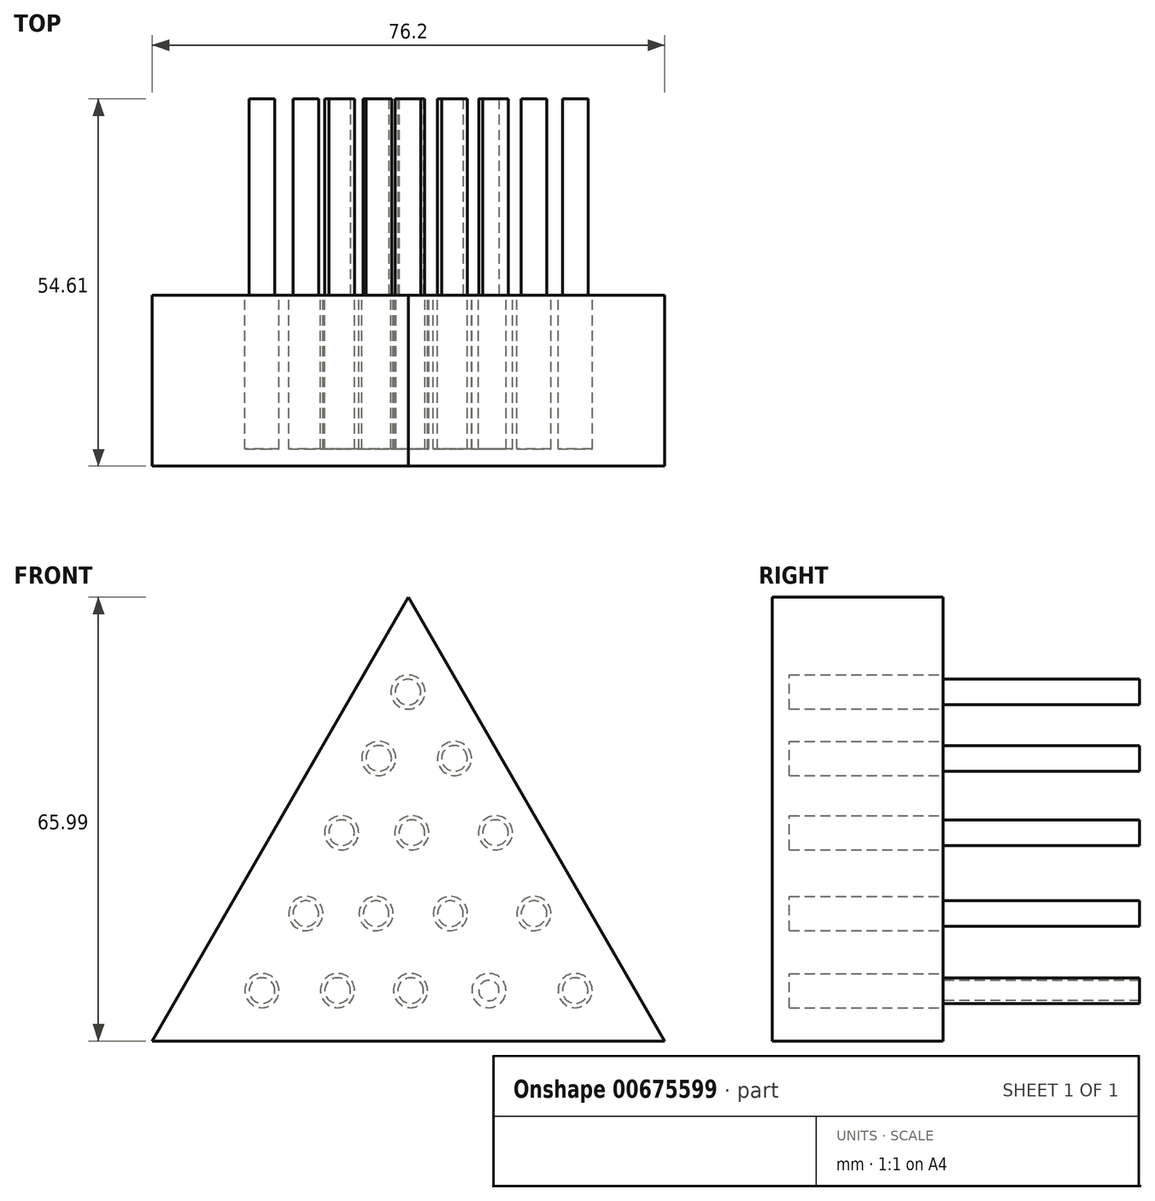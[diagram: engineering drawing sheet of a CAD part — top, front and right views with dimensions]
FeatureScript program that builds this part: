
annotation { "Feature Type Name" : "Feature", "Feature Type Description" : "" }
export const myFeature = defineFeature(function(context is Context, id is Id, definition is map)
    precondition{}
    {
        {
            var Q0;
            Q0=qCreatedBy(makeId("Front.planeOp"),FACE);
            var sketch = newSketch(context, id + "F0", { "sketchPlane" : qUnion([Q0])});
            skLineSegment(sketch, "E0", {"start": v(-76.2, 0) * mm, "end": v(0, 0) * mm});
            skLineSegment(sketch, "E1", {"start": v(0, 0) * mm, "end": v(-38.1, 66) * mm});
            skPoint(sketch, "E1.endSnap0", {"position": v(-38.1, 0) * mm});
            skLineSegment(sketch, "E2", {"start": v(-38.1, 66) * mm, "end": v(-76.2, 0) * mm});
            skSolve(sketch);
        }
        {
            var Q0;
            Q0 = qSketchRegion(id + "F0", true);
            extrude(context, id + "F1", {"entities" : qUnion([Q0]), "depth" : 25.4 * mm, "offsetDistance" : 25.4 * mm});
        }
        {
            var Q0;
            Q0=qCreatedBy(makeId("Front.planeOp"),FACE);
            var sketch = newSketch(context, id + "F2", { "sketchPlane" : qUnion([Q0])});
            skCircle(sketch, "E3", {"center": v(-37.79, 7.5) * mm, "radius": 2.54 * mm});
            skCircle(sketch, "E4", {"center": v(-48.64, 7.5) * mm, "radius": 2.54 * mm});
            skCircle(sketch, "E5", {"center": v(-26.14, 7.5) * mm, "radius": 2.54 * mm});
            skCircle(sketch, "E6", {"center": v(-59.88, 7.5) * mm, "radius": 2.54 * mm});
            skCircle(sketch, "E7", {"center": v(-13.32, 7.5) * mm, "radius": 2.54 * mm});
            skSolve(sketch);
        }
        {
            var Q0;
            Q0 = qSketchRegion(id + "F2", true);
            extrude(context, id + "F3", {"entities" : qUnion([Q0]), "operationType" : NewBodyOperationType.REMOVE, "depth" : 22.86 * mm, "offsetDistance" : 25.4 * mm});
        }
        {
            var Q0;
            Q0=qCreatedBy(makeId("Front.planeOp"),FACE);
            var sketch = newSketch(context, id + "F4", { "sketchPlane" : qUnion([Q0])});
            skCircle(sketch, "E8", {"center": v(-31.87, 18.94) * mm, "radius": 2.54 * mm});
            skCircle(sketch, "E9", {"center": v(-19.44, 18.94) * mm, "radius": 2.54 * mm});
            skCircle(sketch, "E10", {"center": v(-42.92, 18.94) * mm, "radius": 2.54 * mm});
            skCircle(sketch, "E11", {"center": v(-53.37, 18.94) * mm, "radius": 2.54 * mm});
            skSolve(sketch);
        }
        {
            var Q0;
            Q0 = qSketchRegion(id + "F4", true);
            extrude(context, id + "F5", {"entities" : qUnion([Q0]), "operationType" : NewBodyOperationType.REMOVE, "depth" : 22.86 * mm, "offsetDistance" : 25.4 * mm});
        }
        {
            var Q0;
            Q0=qCreatedBy(makeId("Front.planeOp"),FACE);
            var sketch = newSketch(context, id + "F6", { "sketchPlane" : qUnion([Q0])});
            skCircle(sketch, "E12", {"center": v(-25.16, 30.98) * mm, "radius": 2.54 * mm});
            skCircle(sketch, "E13", {"center": v(-37.59, 30.98) * mm, "radius": 2.54 * mm});
            skCircle(sketch, "E14", {"center": v(-48.05, 30.98) * mm, "radius": 2.54 * mm});
            skSolve(sketch);
        }
        {
            var Q0;
            Q0 = qSketchRegion(id + "F6", true);
            extrude(context, id + "F7", {"entities" : qUnion([Q0]), "operationType" : NewBodyOperationType.REMOVE, "depth" : 22.86 * mm, "offsetDistance" : 25.4 * mm});
        }
        {
            var Q0;
            Q0=qCreatedBy(makeId("Front.planeOp"),FACE);
            var sketch = newSketch(context, id + "F8", { "sketchPlane" : qUnion([Q0])});
            skCircle(sketch, "E15", {"center": v(-31.27, 42.03) * mm, "radius": 2.54 * mm});
            skCircle(sketch, "E16", {"center": v(-42.52, 42.03) * mm, "radius": 2.54 * mm});
            skSolve(sketch);
        }
        {
            var Q0;
            Q0 = qSketchRegion(id + "F8", true);
            extrude(context, id + "F9", {"entities" : qUnion([Q0]), "operationType" : NewBodyOperationType.REMOVE, "depth" : 22.86 * mm, "offsetDistance" : 25.4 * mm});
        }
        {
            var Q0;
            Q0=qCreatedBy(makeId("Front.planeOp"),FACE);
            var sketch = newSketch(context, id + "F10", { "sketchPlane" : qUnion([Q0])});
            skCircle(sketch, "E17", {"center": v(-38.18, 51.9) * mm, "radius": 2.54 * mm});
            skSolve(sketch);
        }
        {
            var Q0;
            Q0 = qSketchRegion(id + "F10", true);
            extrude(context, id + "F11", {"entities" : qUnion([Q0]), "operationType" : NewBodyOperationType.REMOVE, "depth" : 22.86 * mm, "offsetDistance" : 25.4 * mm});
        }
        {
            var Q0;
            Q0=makeQuery(id+"F1.opExtrude","CAP_FACE",FACE,{"disambiguationData":[OSD([sQuery(id+"F0.wireOp",EDGE,"E0"),sQuery(id+"F0.wireOp",EDGE,"E1"),sQuery(id+"F0.wireOp",EDGE,"E2")])],"isStart":true});
            var sketch = newSketch(context, id + "F12", { "sketchPlane" : qUnion([Q0])});
            skCircle(sketch, "E18", {"center": v(38.18, 51.9) * mm, "radius": 1.9 * mm});
            skCircle(sketch, "E19", {"center": v(31.27, 42.03) * mm, "radius": 1.9 * mm});
            skCircle(sketch, "E20", {"center": v(42.52, 42.03) * mm, "radius": 1.9 * mm});
            skCircle(sketch, "E21", {"center": v(48.05, 30.98) * mm, "radius": 1.9 * mm});
            skCircle(sketch, "E22", {"center": v(37.59, 30.98) * mm, "radius": 1.9 * mm});
            skCircle(sketch, "E23", {"center": v(25.16, 30.98) * mm, "radius": 1.9 * mm});
            skCircle(sketch, "E24", {"center": v(19.44, 18.94) * mm, "radius": 1.9 * mm});
            skCircle(sketch, "E25", {"center": v(31.87, 18.94) * mm, "radius": 1.9 * mm});
            skCircle(sketch, "E26", {"center": v(42.92, 18.94) * mm, "radius": 1.9 * mm});
            skCircle(sketch, "E27", {"center": v(53.37, 18.94) * mm, "radius": 1.9 * mm});
            skCircle(sketch, "E28", {"center": v(13.32, 7.5) * mm, "radius": 1.9 * mm});
            skCircle(sketch, "E29", {"center": v(26.14, 7.5) * mm, "radius": 1.52 * mm});
            skCircle(sketch, "E30", {"center": v(37.79, 7.5) * mm, "radius": 1.9 * mm});
            skCircle(sketch, "E31", {"center": v(48.64, 7.5) * mm, "radius": 1.9 * mm});
            skCircle(sketch, "E32", {"center": v(59.88, 7.5) * mm, "radius": 1.9 * mm});
            skSolve(sketch);
        }
        {
            var Q0;
            Q0 = qSketchRegion(id + "F12", true);
            extrude(context, id + "F13", {"entities" : qUnion([Q0]), "depth" : 29.2 * mm, "offsetDistance" : 25.4 * mm});
        }
    });
